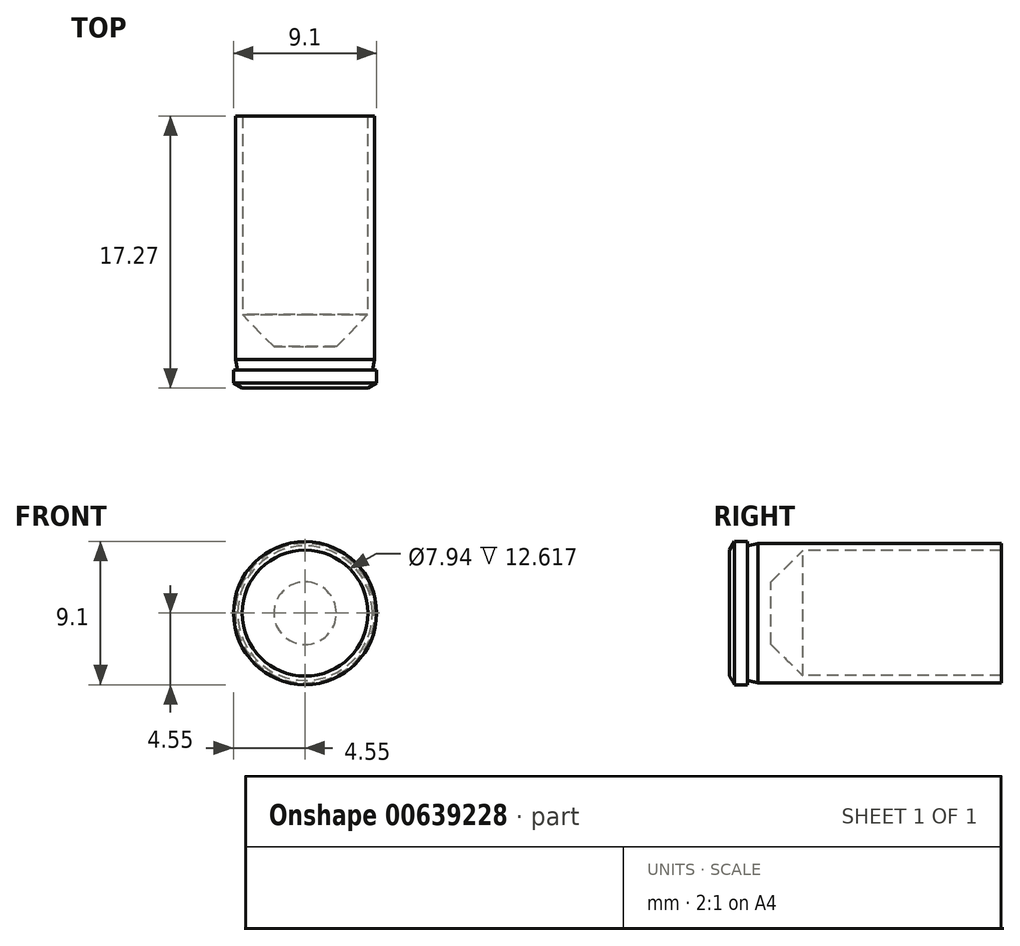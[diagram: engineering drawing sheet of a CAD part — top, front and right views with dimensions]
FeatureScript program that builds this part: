
annotation { "Feature Type Name" : "Feature", "Feature Type Description" : "" }
export const myFeature = defineFeature(function(context is Context, id is Id, definition is map)
    precondition{}
    {
        {
            var Q0;
            Q0=qCreatedBy(makeId("Right.planeOp"),FACE);
            var sketch = newSketch(context, id + "F0", { "sketchPlane" : qUnion([Q0])});
            skLineSegment(sketch, "E0", {"start": v(-20.2, 0) * mm, "end": v(-13.63, 0) * mm, "construction": true});
            skLineSegment(sketch, "E1", {"start": v(-13.63, 0) * mm, "end": v(-13.63, 4) * mm});
            skLineSegment(sketch, "E2", {"start": v(-13.3, 4.55) * mm, "end": v(-12.49, 4.55) * mm});
            skLineSegment(sketch, "E3", {"start": v(-12.49, 4.55) * mm, "end": v(-12.49, 4.28) * mm});
            skLineSegment(sketch, "E4", {"start": v(-11.83, 4.42) * mm, "end": v(3.64, 4.42) * mm});
            skLineSegment(sketch, "E5", {"start": v(-13.3, 4.55) * mm, "end": v(-13.63, 4) * mm});
            skPoint(sketch, "E6.orphan", {"position": v(-13.63, 4.55) * mm});
            skLineSegment(sketch, "E7", {"start": v(4.79, 3.97) * mm, "end": v(4.79, 0) * mm, "construction": true});
            skLineSegment(sketch, "E8", {"start": v(3.64, 4.42) * mm, "end": v(3.64, 3.97) * mm});
            skLineSegment(sketch, "E9", {"start": v(3.64, 3.97) * mm, "end": v(-8.98, 3.97) * mm});
            skLineSegment(sketch, "E10", {"start": v(-11, 1.98) * mm, "end": v(-11, 0) * mm});
            skPoint(sketch, "E11.orphan", {"position": v(-13.63, 0) * mm});
            skPoint(sketch, "E12.orphan", {"position": v(-13.63, 2) * mm});
            skLineSegment(sketch, "E13", {"start": v(-12.49, 4.28) * mm, "end": v(-11.83, 4.43) * mm});
            skLineSegment(sketch, "E14", {"start": v(-8.98, 3.97) * mm, "end": v(-11, 1.98) * mm});
            skPoint(sketch, "E15.orphan", {"position": v(-11, 3.97) * mm});
            skLineSegment(sketch, "E16.trimOffspring", {"start": v(-11, 0) * mm, "end": v(33.89, 0) * mm, "construction": true});
            skPoint(sketch, "E17.orphan", {"position": v(-12.17, 0) * mm});
            skLineSegment(sketch, "E18", {"start": v(-13.63, 0) * mm, "end": v(-11, 0) * mm});
            skSolve(sketch);
        }
        {
            var Q0;
            Q0=makeQuery(id+"F0.imprint","IMPRINT",FACE,{"disambiguationData":[TD([[makeQuery(id+"F0.imprint","IMPRINT",EDGE,{"derivedFrom":sQuery(id+"F0.wireOp",EDGE,"E1")}),-1.0]])]});
            var Q1;
            Q1=sQuery(id+"F0.wireOp",EDGE,"E0");
            revolve(context, id + "F1", {"entities" : qUnion([Q0]), "axis" : qUnion([Q1]), "revolveType" : RevolveType.FULL});
        }
    });
